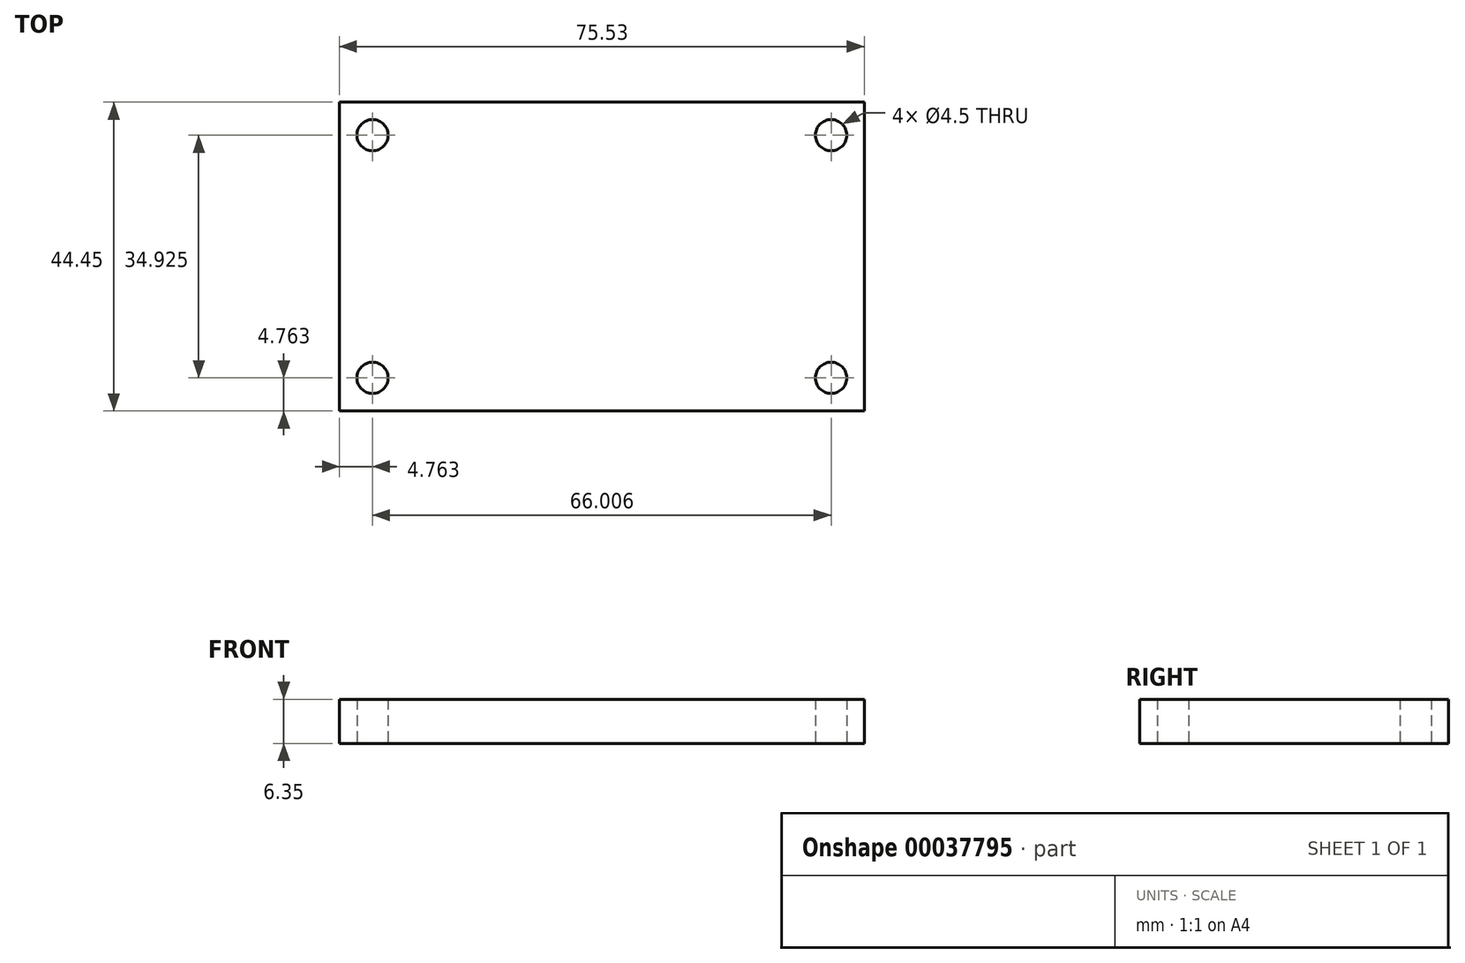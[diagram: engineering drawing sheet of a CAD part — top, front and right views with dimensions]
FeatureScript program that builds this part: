
annotation { "Feature Type Name" : "Feature", "Feature Type Description" : "" }
export const myFeature = defineFeature(function(context is Context, id is Id, definition is map)
    precondition{}
    {
        {
            var Q0;
            Q0=qCreatedBy(makeId("Top.planeOp"),FACE);
            var sketch = newSketch(context, id + "F0", { "sketchPlane" : qUnion([Q0])});
            skLineSegment(sketch, "E0.bottom", {"start": v(0, 0) * mm, "end": v(75.53, 0) * mm});
            skLineSegment(sketch, "E0.top", {"start": v(0, -44.45) * mm, "end": v(75.53, -44.45) * mm});
            skLineSegment(sketch, "E0.left", {"start": v(0, 0) * mm, "end": v(0, -44.45) * mm});
            skLineSegment(sketch, "E0.right", {"start": v(75.53, 0) * mm, "end": v(75.53, -44.45) * mm});
            skLineSegment(sketch, "E1.top", {"start": v(0, -4.76) * mm, "end": v(4.76, -4.76) * mm, "construction": true});
            skLineSegment(sketch, "E1.right", {"start": v(4.76, 0) * mm, "end": v(4.76, -4.76) * mm, "construction": true});
            skLineSegment(sketch, "E2.top", {"start": v(75.53, -4.76) * mm, "end": v(70.77, -4.76) * mm, "construction": true});
            skLineSegment(sketch, "E2.right", {"start": v(70.77, 0) * mm, "end": v(70.77, -4.76) * mm, "construction": true});
            skLineSegment(sketch, "E3", {"start": v(4.76, -44.45) * mm, "end": v(4.76, -39.69) * mm, "construction": true});
            skLineSegment(sketch, "E4", {"start": v(70.77, -44.45) * mm, "end": v(70.77, -39.69) * mm, "construction": true});
            skCircle(sketch, "E5", {"center": v(4.76, -4.76) * mm, "radius": 2.25 * mm});
            skCircle(sketch, "E6", {"center": v(4.76, -39.69) * mm, "radius": 2.25 * mm});
            skCircle(sketch, "E7", {"center": v(70.77, -39.69) * mm, "radius": 2.25 * mm});
            skCircle(sketch, "E8", {"center": v(70.77, -4.76) * mm, "radius": 2.25 * mm});
            skSolve(sketch);
        }
        {
            var Q0;
            Q0 = qSketchRegion(id + "F0", true);
            extrude(context, id + "F1", {"entities" : qUnion([Q0]), "depth" : 6.35 * mm});
        }
    });
